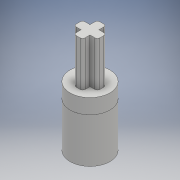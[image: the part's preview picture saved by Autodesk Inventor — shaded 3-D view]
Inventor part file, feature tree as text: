
AUTODESK INVENTOR PART (.ipt)
format: ipt  version: 2018.2 (Build 222227000, 227)  size: 155,648 bytes
history: native  units: mm
features: extrude x4, fillet x4, sketch x4
ambient origin geometry x8: Origin, YZ Plane, XZ Plane, XY Plane, X Axis, Y Axis, Z Axis, Center Point
bodies: Solid1 (feature_tree)
feature tree (12):
  extrude  "Extrusion1"  Depth=8.0mm
  extrude  "Extrusion2"  Depth=3.0mm TaperAngle=0.0deg
  extrude  "Extrusion3"  Depth=1.8mm
  fillet  "Fillet1"  Radius=2.4mm
  fillet  "Fillet2"  Radius=1.8mm
  fillet  "Fillet3"  Radius=4.8mm
  fillet  "Fillet4"  Radius=2.4mm
  extrude  "Extrusion4"  Depth=0.5mm
  sketch  "Sketch1"  dims[d0=4.5mm d1=8.0mm]
  sketch  "Sketch2"  dims[d2=9.0mm d3=0.0mm d4=3.0mm d5=0.0mm]
  sketch  "Sketch3"  dims[d6=4.8mm d7=1.8mm d8=2.4mm d10=1.8mm d11=4.8mm d12=2.4mm]
  sketch  "Sketch5"  dims[d14=9.0mm d15=0.0mm d19=0.5mm d20=0.5mm d21=0.5mm d22=0.5mm d23=10.0mm d24=0.0mm]
